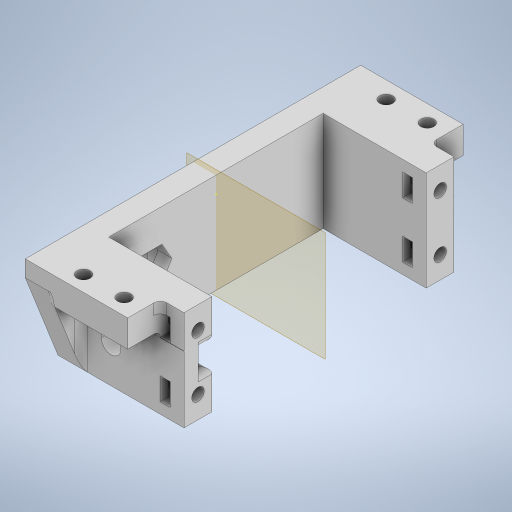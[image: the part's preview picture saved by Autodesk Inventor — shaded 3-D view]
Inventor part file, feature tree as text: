
AUTODESK INVENTOR PART (.ipt)
format: ipt  version: 2024 (Build 280153020, 153B)  size: 493,056 bytes
history: native  units: mm
features: sketch x13, extrude x11, fillet x2, projected_geometry x2, plane x1, mirror x1, hole x1
ambient origin geometry x8: Origin, YZ Plane, XZ Plane, XY Plane, X Axis, Y Axis, Z Axis, Center Point
bodies: Body1 (feature_tree)
feature tree (31):
  extrude  "Extrusion2"  Depth=82.5mm
  extrude  "Extrusion3"  Depth=65.5mm
  extrude  "Extrusion4"  Depth=8.5mm
  extrude  "Extrusion6"  Depth=8.5mm
  extrude  "Extrusion7"  Depth=31.5mm TaperAngle=0.0deg
  sketch  "Sketch10"  dims[d17=23.5mm d18=0.0mm d19=7.0mm d20=0.0mm]
  sketch  "Sketch12"  dims[d25=13.2mm d26=5.25mm]
  extrude  "Extrusion12"  Depth=7.0mm TaperAngle=0.0deg
  extrude  "Extrusion13"  Depth=5.25mm
  plane  "Work Plane1"
  mirror  "Mirror1"
  extrude  "Extrusion14"  Depth=5.75mm
  sketch  "Sketch19"  dims[d49=4.2mm d61=4.2mm d62=3.4mm]
  extrude  "Extrusion15"  Depth=3.25mm
  fillet  "Fillet4"  Radius=4.2mm
  extrude  "Extrusion16"  Depth=3.25mm
  extrude  "Extrusion17"  Depth=4.2mm
  fillet  "Fillet5"  Radius=3.4mm
  hole  "Hole3"  [1 undecoded]
  sketch  "Sketch2"  dims[d0=30.5mm d1=82.5mm]
  sketch  "Sketch4"  dims[d2=30.5mm d3=65.5mm]
  sketch  "Sketch5"  dims[d4=4.25mm d6=8.5mm]
  sketch  "Sketch8"  dims[d7=8.5mm d8=8.5mm]
  sketch  "Sketch9"  dims[d14=3.8mm d15=31.5mm d16=0.0mm]
  sketch  "Sketch13"  dims[d27=4.2mm d28=0.0mm d29=5.75mm]
  sketch  "Sketch16"  dims[d30=0.0mm d31=0.0mm d44=3.25mm d46=4.2mm]
  sketch  "Sketch18"  dims[d47=3.25mm d48=3.25mm]
  sketch  "Sketch20"  dims[d63=3.0mm d64=6.8mm]
  projected_geometry  "Projected Loop1"
  projected_geometry  "Projected Loop2"
  sketch  "Sketch21"  dims[d65=3.0mm d66=3.4mm d70=73.6mm d71=0.0mm d72=8.1mm d73=0.0mm d76=5.0mm d77=10.0mm d78=0.0mm d80=7.0mm d81=0.0mm d90=3.25mm d91=0.0mm d92=2.0mm d93=0.0mm d94=0.0mm d95=10.0mm d96=0.0mm d97=2.0mm d105=4.0mm d106=6.0mm d107=9.2mm d108=2.0mm d109=90.0deg d110=8.0mm d111=20.594885mm]
note: 1 required parameter value undecoded (feature->parameter linkage not recoverable at this tier; creation-order binding heuristic only, values carry confidence <= 0.55)
